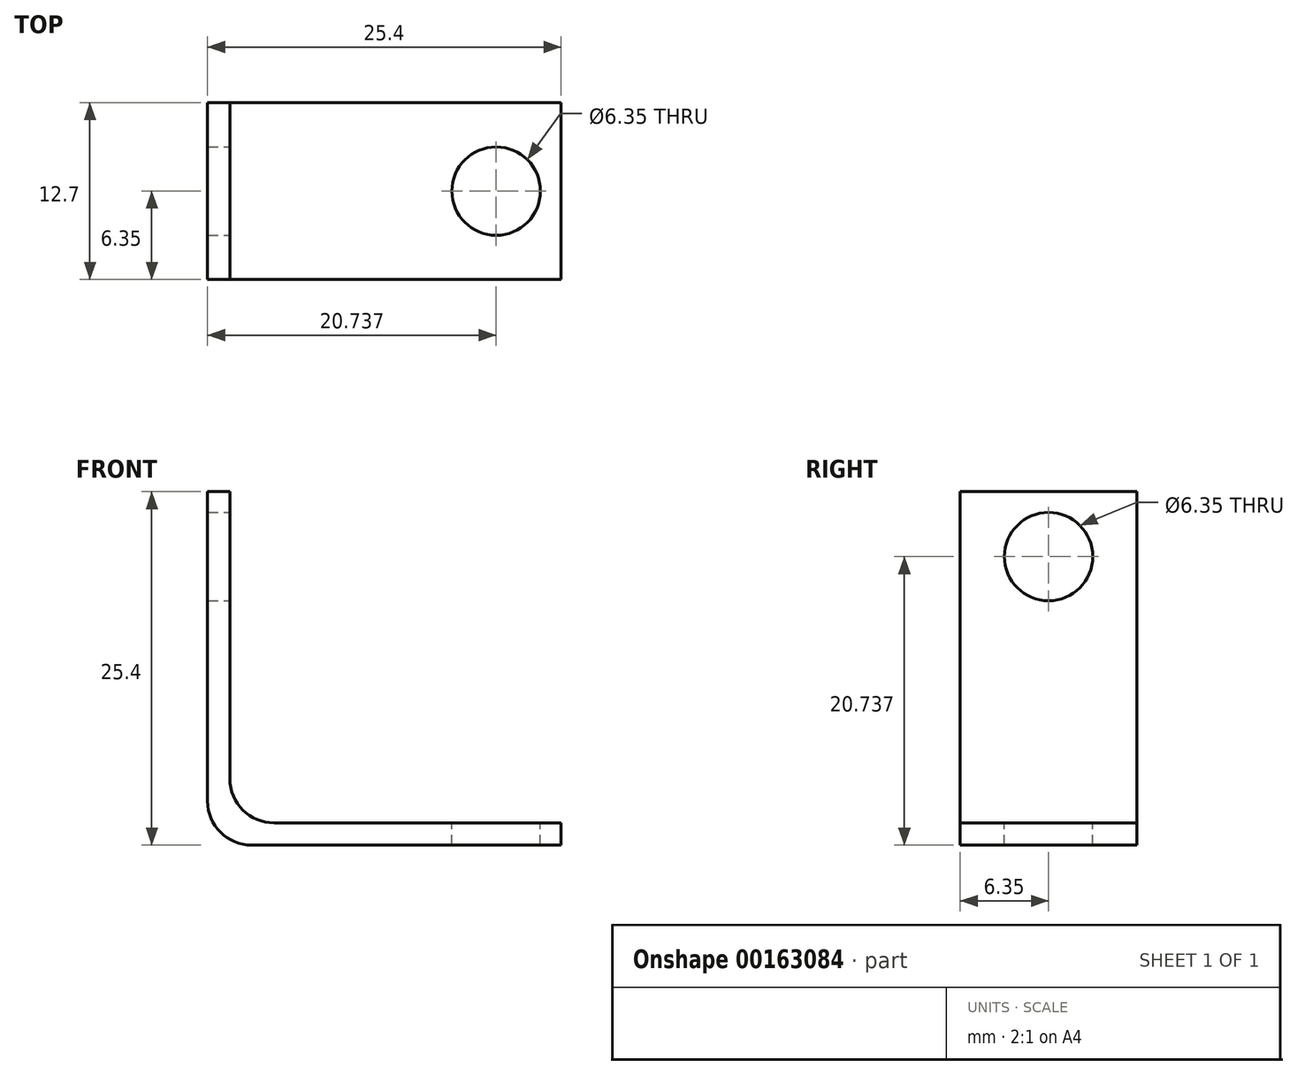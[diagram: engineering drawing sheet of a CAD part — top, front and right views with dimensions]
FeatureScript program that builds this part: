
annotation { "Feature Type Name" : "Feature", "Feature Type Description" : "" }
export const myFeature = defineFeature(function(context is Context, id is Id, definition is map)
    precondition{}
    {
        {
            var Q0;
            Q0=qCreatedBy(makeId("Front.planeOp"),FACE);
            var sketch = newSketch(context, id + "F0", { "sketchPlane" : qUnion([Q0])});
            skLineSegment(sketch, "E0", {"start": v(0, 3.18) * mm, "end": v(0, 25.4) * mm});
            skLineSegment(sketch, "E1", {"start": v(3.18, 0) * mm, "end": v(25.4, 0) * mm});
            skLineSegment(sketch, "E2", {"start": v(25.4, 0) * mm, "end": v(25.4, 1.6) * mm});
            skLineSegment(sketch, "E3", {"start": v(25.4, 1.6) * mm, "end": v(4.78, 1.6) * mm});
            skLineSegment(sketch, "E4", {"start": v(0, 25.4) * mm, "end": v(1.6, 25.4) * mm});
            skLineSegment(sketch, "E5", {"start": v(1.6, 25.4) * mm, "end": v(1.6, 4.78) * mm});
            skPoint(sketch, "E6.visualSharp", {"position": v(1.6, 1.6) * mm});
            skArc(sketch, "E6.filletArc", {"start": v(1.6, 4.78) * mm, "mid": v(2.53, 2.53) * mm, "end": v(4.78, 1.6) * mm});
            skPoint(sketch, "E7.visualSharp", {"position": v(0, 0) * mm});
            skArc(sketch, "E7.filletArc", {"start": v(0, 3.18) * mm, "mid": v(0.93, 0.93) * mm, "end": v(3.18, 0) * mm});
            skSolve(sketch);
        }
        {
            var Q0;
            Q0 = qSketchRegion(id + "F0", true);
            extrude(context, id + "F1", {"entities" : qUnion([Q0]), "depth" : 12.7 * mm});
        }
        {
            var Q0;
            Q0=makeQuery(id+"F1.opExtrude","SWEPT_FACE",FACE,{"disambiguationData":[OSD([sQuery(id+"F0.wireOp",EDGE,"E3")])]});
            var sketch = newSketch(context, id + "F2", { "sketchPlane" : qUnion([Q0])});
            skCircle(sketch, "E8", {"center": v(20.74, -6.35) * mm, "radius": 3.18 * mm});
            skSolve(sketch);
        }
        {
            var Q0;
            Q0 = qSketchRegion(id + "F2", true);
            extrude(context, id + "F3", {"entities" : qUnion([Q0]), "operationType" : NewBodyOperationType.REMOVE, "oppositeDirection" : true, "depth" : 25.4 * mm});
        }
        {
            var Q0;
            Q0=makeQuery(id+"F1.opExtrude","SWEPT_FACE",FACE,{"disambiguationData":[OSD([sQuery(id+"F0.wireOp",EDGE,"E5")])]});
            var sketch = newSketch(context, id + "F4", { "sketchPlane" : qUnion([Q0])});
            skCircle(sketch, "E9", {"center": v(-6.35, 20.74) * mm, "radius": 3.18 * mm});
            skSolve(sketch);
        }
        {
            var Q0;
            Q0 = qSketchRegion(id + "F4", true);
            extrude(context, id + "F5", {"entities" : qUnion([Q0]), "operationType" : NewBodyOperationType.REMOVE, "oppositeDirection" : true, "depth" : 25.4 * mm});
        }
    });
